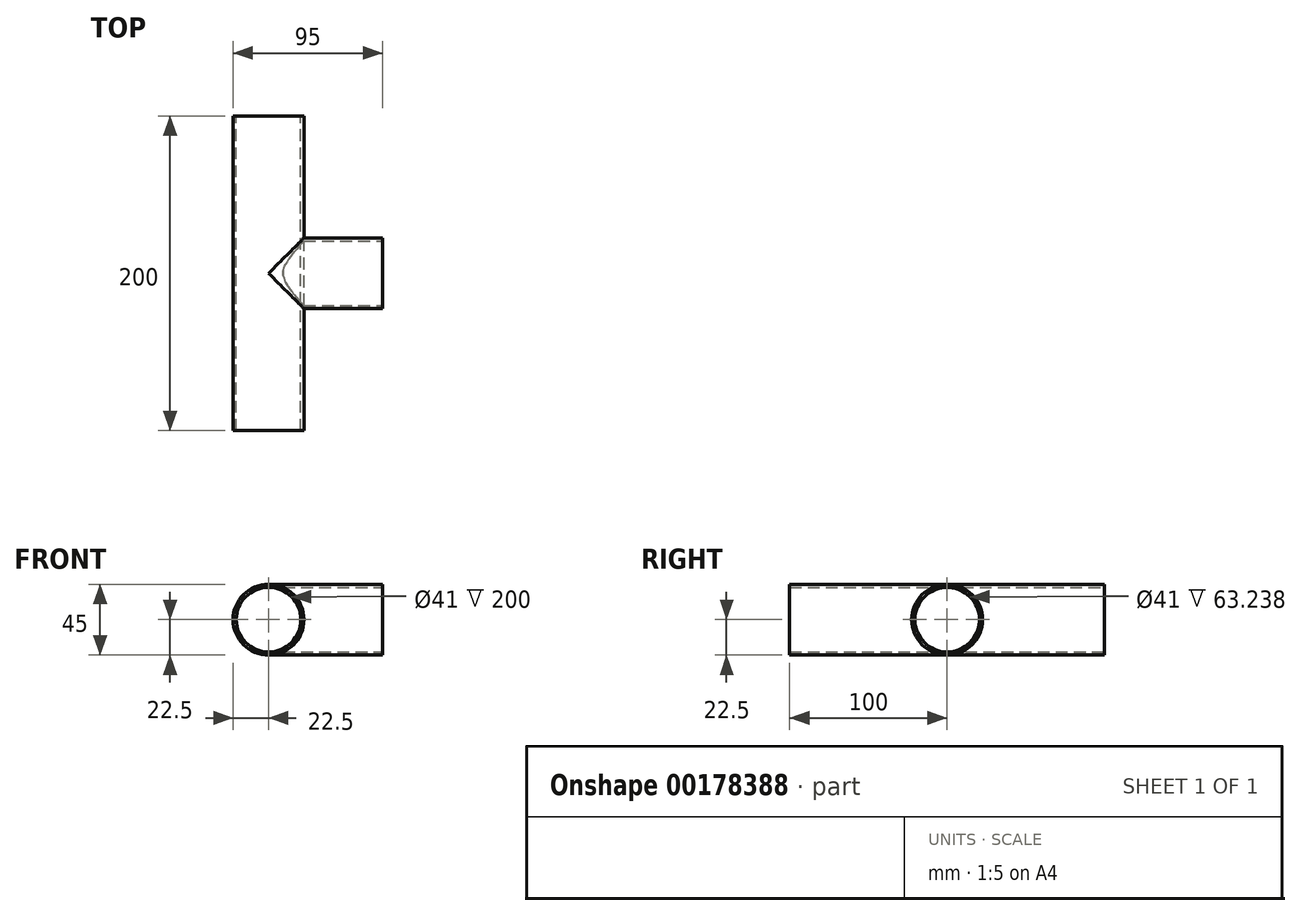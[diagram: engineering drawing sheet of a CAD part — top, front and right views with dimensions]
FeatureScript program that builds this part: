
annotation { "Feature Type Name" : "Feature", "Feature Type Description" : "" }
export const myFeature = defineFeature(function(context is Context, id is Id, definition is map)
    precondition{}
    {
        {
            var Q0;
            Q0=qCreatedBy(makeId("Front.planeOp"),FACE);
            var sketch = newSketch(context, id + "F0", { "sketchPlane" : qUnion([Q0])});
            skCircle(sketch, "E0", {"center": v(0, 0) * mm, "radius": 22.5 * mm});
            skCircle(sketch, "E1.0", {"center": v(0, 0) * mm, "radius": 20.5 * mm});
            skSolve(sketch);
        }
        {
            var Q0;
            Q0=makeQuery(id+"F0.imprint","IMPRINT",FACE,{"disambiguationData":[TD([[makeQuery(id+"F0.imprint","IMPRINT",EDGE,{"derivedFrom":sQuery(id+"F0.wireOp",EDGE,"E0")}),1.0]])]});
            extrude(context, id + "F1", {"entities" : qUnion([Q0]), "depth" : 200 * mm});
        }
        {
            var Q0;
            Q0=qCreatedBy(makeId("Right.planeOp"),FACE);
            cPlane(context, id + "F2", {"entities" : qUnion([Q0]), "cplaneType" : CPlaneType.OFFSET, "offset" : 72.5 * mm, "width" : 150 * mm, "height" : 150 * mm});
        }
        {
            var Q0;
            Q0=qCreatedBy(id+"F2.planeOp",FACE);
            var sketch = newSketch(context, id + "F3", { "sketchPlane" : qUnion([Q0])});
            skLineSegment(sketch, "E2.0", {"start": v(0, -22.5) * mm, "end": v(0, 22.5) * mm});
            skLineSegment(sketch, "E3.0", {"start": v(-200, -22.5) * mm, "end": v(-200, 22.5) * mm});
            skLineSegment(sketch, "E4", {"start": v(-200, 22.5) * mm, "end": v(0, 22.5) * mm});
            skLineSegment(sketch, "E5", {"start": v(0, -22.5) * mm, "end": v(-200, -22.5) * mm});
            skPoint(sketch, "E6", {"position": v(-100, 0) * mm});
            skPoint(sketch, "E6.positionSnap0", {"position": v(-100, -22.5) * mm});
            skLineSegment(sketch, "E7", {"start": v(-100, 41.5) * mm, "end": v(-100, -55.14) * mm});
            skCircle(sketch, "E8", {"center": v(-100, 0) * mm, "radius": 22.5 * mm});
            skCircle(sketch, "E9.0", {"center": v(-100, 0) * mm, "radius": 20.5 * mm});
            skSolve(sketch);
        }
        {
            var Q0;
            {var subQ1=sQuery(id+"F3.wireOp",EDGE,"E7");var subQ3=sQuery(id+"F3.wireOp",EDGE,"E9.0");var subQ4=makeQuery(id+"F3.imprint","INTERSECT",VERTEX,{"disambiguationData":[OD(0.0)],"derivedFrom":[subQ1,subQ3]});Q0=makeQuery(id+"F3.imprint","IMPRINT",FACE,{"disambiguationData":[TD([[makeQuery(id+"F3.imprint","IMPRINT",EDGE,{"disambiguationData":[TD([[subQ4,-1.0]])],"derivedFrom":subQ3}),-1.0]])]});}
            var Q1;
            {var subQ1=sQuery(id+"F3.wireOp",EDGE,"E7");var subQ3=sQuery(id+"F3.wireOp",EDGE,"E9.0");var subQ4=makeQuery(id+"F3.imprint","INTERSECT",VERTEX,{"disambiguationData":[OD(0.0)],"derivedFrom":[subQ1,subQ3]});Q1=makeQuery(id+"F3.imprint","IMPRINT",FACE,{"disambiguationData":[TD([[makeQuery(id+"F3.imprint","IMPRINT",EDGE,{"disambiguationData":[TD([[subQ4,1.0]])],"derivedFrom":subQ3}),-1.0]])]});}
            extrude(context, id + "F4", {"entities" : qUnion([Q0, Q1]), "operationType" : NewBodyOperationType.ADD, "endBound" : BoundingType.UP_TO_NEXT, "oppositeDirection" : true, "depth" : 25 * mm});
        }
    });
